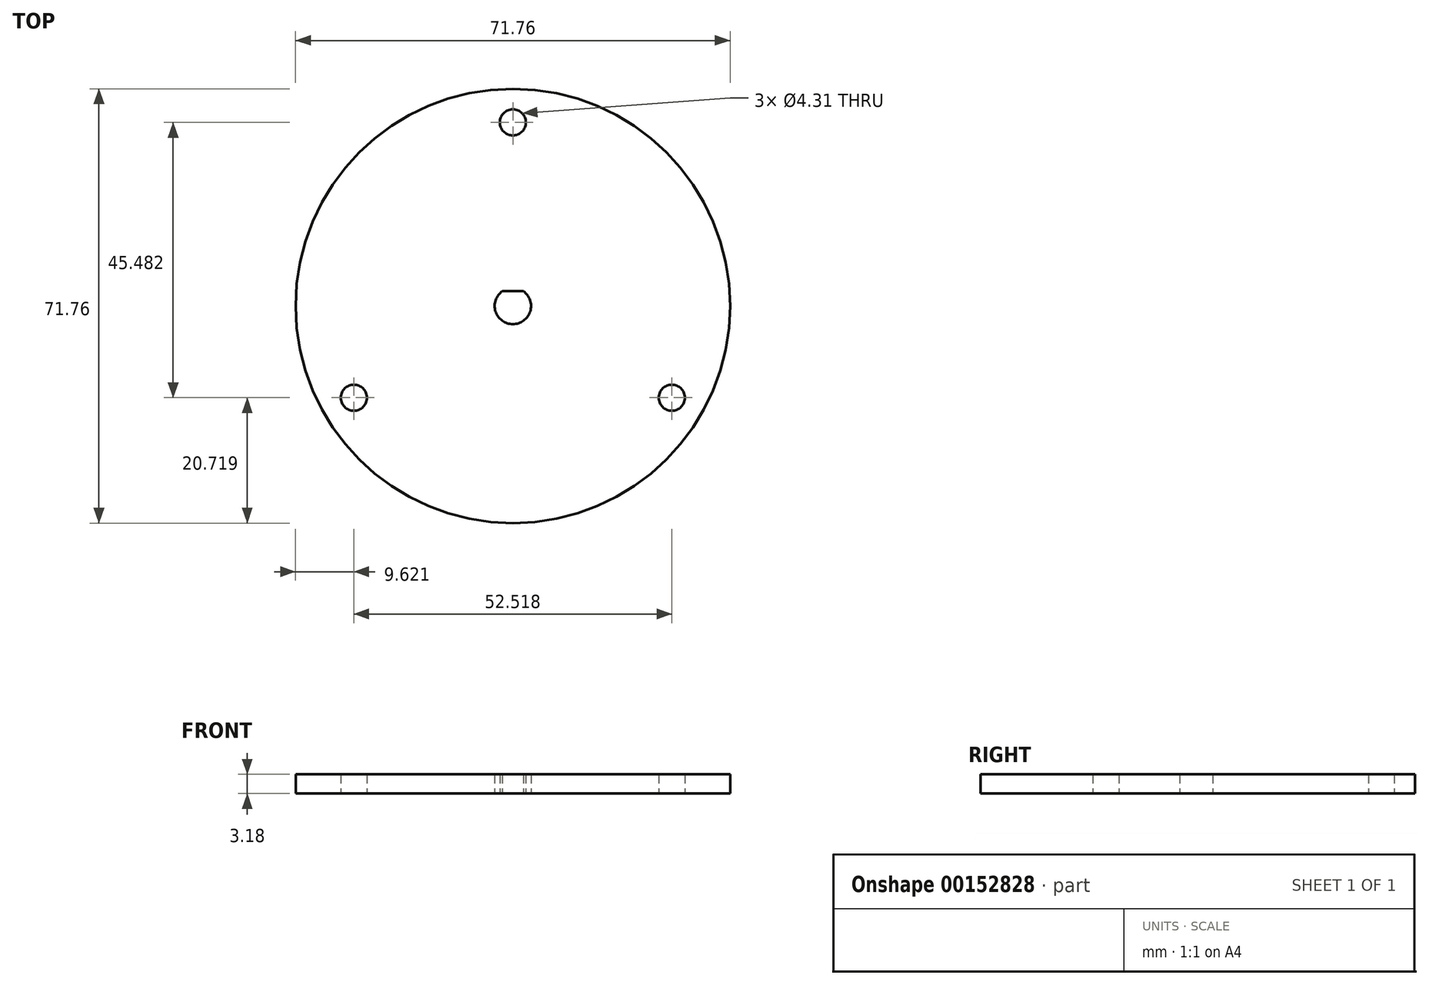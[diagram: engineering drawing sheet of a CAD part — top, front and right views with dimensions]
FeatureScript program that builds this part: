
annotation { "Feature Type Name" : "Feature", "Feature Type Description" : "" }
export const myFeature = defineFeature(function(context is Context, id is Id, definition is map)
    precondition{}
    {
        {
            var Q0;
            Q0=qCreatedBy(makeId("Top.planeOp"),FACE);
            var sketch = newSketch(context, id + "F0", { "sketchPlane" : qUnion([Q0])});
            skArc(sketch, "E0", {"start": v(-1.72, 2.46) * mm, "mid": v(0, -3) * mm, "end": v(1.72, 2.46) * mm});
            skLineSegment(sketch, "E1", {"start": v(-1.72, 2.46) * mm, "end": v(1.72, 2.46) * mm});
            skLineSegment(sketch, "E2", {"start": v(0, 2.46) * mm, "end": v(0, 0) * mm, "construction": true});
            skCircle(sketch, "E3", {"center": v(0, 0) * mm, "radius": 35.88 * mm});
            skCircle(sketch, "E4.cCircle", {"center": v(0, 0) * mm, "radius": 15.16 * mm, "construction": true});
            skLineSegment(sketch, "E4.0", {"start": v(26.26, -15.16) * mm, "end": v(-26.26, -15.16) * mm, "construction": true});
            skLineSegment(sketch, "E4.1", {"start": v(-26.26, -15.16) * mm, "end": v(0, 30.32) * mm, "construction": true});
            skLineSegment(sketch, "E4.2", {"start": v(0, 30.32) * mm, "end": v(26.26, -15.16) * mm, "construction": true});
            skCircle(sketch, "E5", {"center": v(0, 30.32) * mm, "radius": 2.15 * mm});
            skCircle(sketch, "E6", {"center": v(26.26, -15.16) * mm, "radius": 2.15 * mm});
            skCircle(sketch, "E7", {"center": v(-26.26, -15.16) * mm, "radius": 2.15 * mm});
            skSolve(sketch);
        }
        {
            var Q0;
            Q0=qSketchRegion(id+"F0",true);
            extrude(context, id + "F1", {"entities" : qUnion([Q0]), "depth" : 3.17 * mm});
        }
    });
